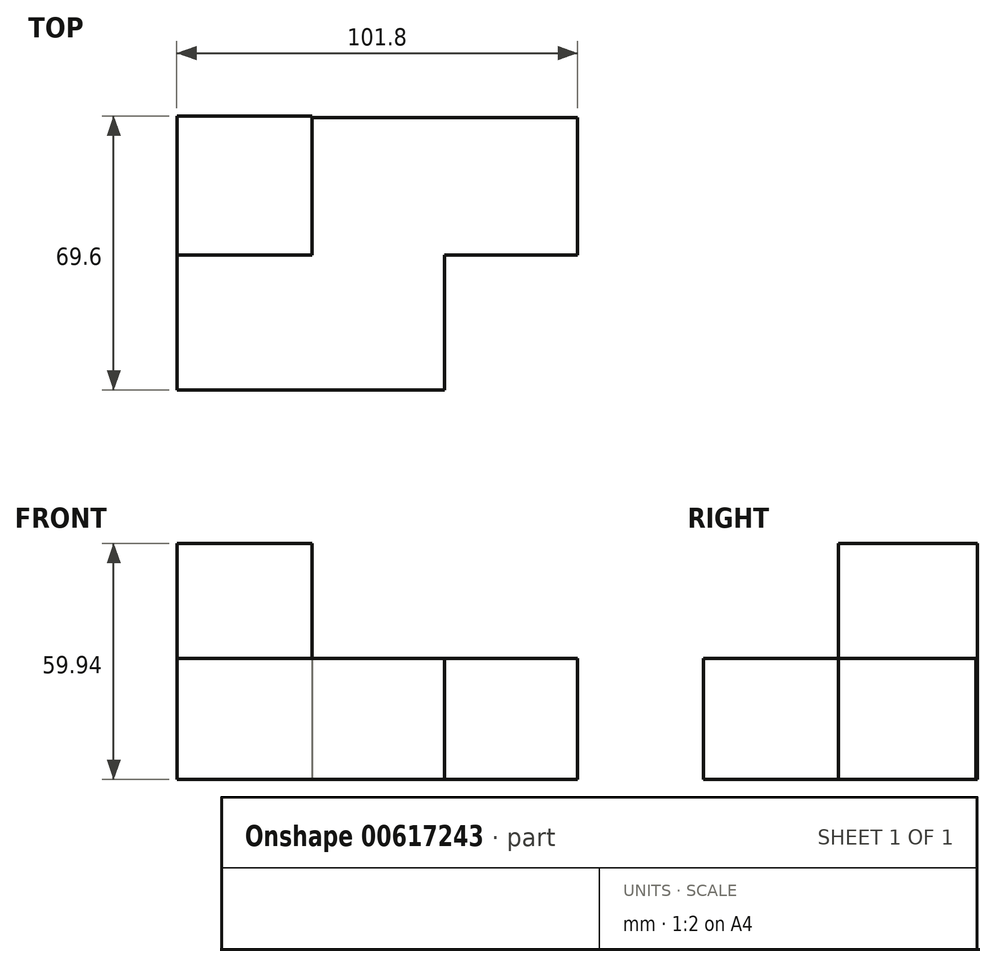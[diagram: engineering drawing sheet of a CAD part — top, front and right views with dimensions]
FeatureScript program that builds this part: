
annotation { "Feature Type Name" : "Feature", "Feature Type Description" : "" }
export const myFeature = defineFeature(function(context is Context, id is Id, definition is map)
    precondition{}
    {
        {
            var Q0;
            Q0=qCreatedBy(makeId("Top.planeOp"),FACE);
            var sketch = newSketch(context, id + "F0", { "sketchPlane" : qUnion([Q0])});
            skLineSegment(sketch, "E0.bottom", {"start": v(-122.91, 56.61) * mm, "end": v(-77.2, 56.61) * mm});
            skLineSegment(sketch, "E0.top", {"start": v(-122.91, -59.5) * mm, "end": v(-77.2, -59.5) * mm});
            skLineSegment(sketch, "E0.left", {"start": v(-122.91, 56.61) * mm, "end": v(-122.91, -59.5) * mm});
            skLineSegment(sketch, "E0.right", {"start": v(-77.2, 56.61) * mm, "end": v(-77.2, -59.5) * mm});
            skLineSegment(sketch, "E1.bottom", {"start": v(-77.2, 56.61) * mm, "end": v(-27.52, 56.61) * mm});
            skLineSegment(sketch, "E1.top", {"start": v(-77.2, -59.5) * mm, "end": v(-27.52, -59.5) * mm});
            skLineSegment(sketch, "E1.right", {"start": v(-27.52, 56.61) * mm, "end": v(-27.52, -59.5) * mm});
            skLineSegment(sketch, "E2.bottom", {"start": v(-27.52, 0) * mm, "end": v(17.94, 0) * mm});
            skLineSegment(sketch, "E2.top", {"start": v(-27.52, -59.5) * mm, "end": v(17.94, -59.5) * mm});
            skLineSegment(sketch, "E2.left", {"start": v(-27.52, 0) * mm, "end": v(-27.52, -59.5) * mm});
            skLineSegment(sketch, "E2.right", {"start": v(17.94, 0) * mm, "end": v(17.94, -59.5) * mm});
            skSolve(sketch);
        }
        {
            var Q0;
            Q0=makeQuery(id+"F0.imprint","IMPRINT",FACE,{"disambiguationData":[TD([[makeQuery(id+"F0.imprint","IMPRINT",EDGE,{"derivedFrom":sQuery(id+"F0.wireOp",EDGE,"E1.bottom")}),-1.0]])]});
            var Q1;
            Q1=makeQuery(id+"F0.imprint","IMPRINT",FACE,{"disambiguationData":[TD([[makeQuery(id+"F0.imprint","IMPRINT",EDGE,{"derivedFrom":sQuery(id+"F0.wireOp",EDGE,"E2.bottom")}),-1.0]])]});
            var Q2;
            Q2=makeQuery(id+"F0.imprint","IMPRINT",FACE,{"disambiguationData":[TD([[makeQuery(id+"F0.imprint","IMPRINT",EDGE,{"derivedFrom":sQuery(id+"F0.wireOp",EDGE,"E0.bottom")}),-1.0]])]});
            extrude(context, id + "F1", {"entities" : qUnion([Q0, Q1, Q2]), "depth" : 38.6 * mm, "offsetDistance" : 25.4 * mm});
        }
        {
            var Q0;
            Q0=makeQuery(id+"F1.opExtrude","CAP_FACE",FACE,{"disambiguationData":[OSD([sQuery(id+"F0.wireOp",EDGE,"E0.bottom"),sQuery(id+"F0.wireOp",EDGE,"E0.top"),sQuery(id+"F0.wireOp",EDGE,"E0.left"),sQuery(id+"F0.wireOp",EDGE,"E1.bottom"),sQuery(id+"F0.wireOp",EDGE,"E1.top"),sQuery(id+"F0.wireOp",EDGE,"E1.right"),sQuery(id+"F0.wireOp",EDGE,"E2.bottom"),sQuery(id+"F0.wireOp",EDGE,"E2.top"),sQuery(id+"F0.wireOp",EDGE,"E2.right")])],"isStart":false});
            var sketch = newSketch(context, id + "F2", { "sketchPlane" : qUnion([Q0])});
            skLineSegment(sketch, "E3.bottom", {"start": v(-122.91, -59.5) * mm, "end": v(-77.24, -59.5) * mm});
            skLineSegment(sketch, "E3.top", {"start": v(-122.91, 0) * mm, "end": v(-77.24, 0) * mm});
            skLineSegment(sketch, "E3.left", {"start": v(-122.91, -59.5) * mm, "end": v(-122.91, 0) * mm});
            skLineSegment(sketch, "E3.right", {"start": v(-77.24, -59.5) * mm, "end": v(-77.24, 0) * mm});
            skSolve(sketch);
        }
        {
            var Q0;
            Q0 = qSketchRegion(id + "F2", true);
            extrude(context, id + "F3", {"entities" : qUnion([Q0]), "operationType" : NewBodyOperationType.ADD, "depth" : 35.3 * mm, "offsetDistance" : 25.4 * mm});
        }
        {
            var Q0;
            Q0=makeQuery(id+"F1.opExtrude","SWEPT_BODY",BODY,{"disambiguationData":[OSD([sQuery(id+"F0.wireOp",EDGE,"E0.bottom"),sQuery(id+"F0.wireOp",EDGE,"E0.top"),sQuery(id+"F0.wireOp",EDGE,"E0.left"),sQuery(id+"F0.wireOp",EDGE,"E1.bottom"),sQuery(id+"F0.wireOp",EDGE,"E1.top"),sQuery(id+"F0.wireOp",EDGE,"E1.right"),sQuery(id+"F0.wireOp",EDGE,"E2.bottom"),sQuery(id+"F0.wireOp",EDGE,"E2.top"),sQuery(id+"F0.wireOp",EDGE,"E2.right")])]});
            deleteBodies(context, id + "F4", {"entities" : qUnion([Q0])});
        }
        {
            var Q0;
            Q0=qCreatedBy(makeId("Top.planeOp"),FACE);
            var sketch = newSketch(context, id + "F5", { "sketchPlane" : qUnion([Q0])});
            skLineSegment(sketch, "E4.bottom", {"start": v(0, 0) * mm, "end": v(-34.22, 0) * mm});
            skLineSegment(sketch, "E4.top", {"start": v(0, 35.28) * mm, "end": v(-34.22, 35.28) * mm});
            skLineSegment(sketch, "E4.left", {"start": v(0, 0) * mm, "end": v(0, 35.28) * mm});
            skLineSegment(sketch, "E4.right", {"start": v(-34.22, 0) * mm, "end": v(-34.22, 35.28) * mm});
            skLineSegment(sketch, "E5.bottom", {"start": v(0, 0) * mm, "end": v(-34.32, 0) * mm});
            skLineSegment(sketch, "E5.top", {"start": v(0, -34.32) * mm, "end": v(-34.32, -34.32) * mm});
            skLineSegment(sketch, "E5.left", {"start": v(0, 0) * mm, "end": v(0, -34.32) * mm});
            skLineSegment(sketch, "E5.right", {"start": v(-34.32, 0) * mm, "end": v(-34.32, -34.32) * mm});
            skLineSegment(sketch, "E6.bottom", {"start": v(0, 0) * mm, "end": v(33.7, 0) * mm});
            skLineSegment(sketch, "E6.top", {"start": v(0, 34.92) * mm, "end": v(33.7, 34.92) * mm});
            skLineSegment(sketch, "E6.left", {"start": v(0, 0) * mm, "end": v(0, 34.92) * mm});
            skLineSegment(sketch, "E6.right", {"start": v(33.7, 0) * mm, "end": v(33.7, 34.92) * mm});
            skLineSegment(sketch, "E7.top", {"start": v(0, -34.32) * mm, "end": v(33.7, -34.32) * mm});
            skLineSegment(sketch, "E7.right", {"start": v(33.7, 0) * mm, "end": v(33.7, -34.32) * mm});
            skPoint(sketch, "E8.oppositeSnap0", {"position": v(16.85, 34.92) * mm});
            skLineSegment(sketch, "E8.bottom", {"start": v(33.7, 0) * mm, "end": v(67.48, 0) * mm});
            skLineSegment(sketch, "E8.top", {"start": v(33.7, 34.92) * mm, "end": v(67.48, 34.92) * mm});
            skLineSegment(sketch, "E8.right", {"start": v(67.48, 0) * mm, "end": v(67.48, 34.92) * mm});
            skSolve(sketch);
        }
        {
            var Q0;
            Q0=makeQuery(id+"F5.imprint","IMPRINT",FACE,{"disambiguationData":[TD([[makeQuery(id+"F5.imprint","IMPRINT",EDGE,{"derivedFrom":sQuery(id+"F5.wireOp",EDGE,"E4.top")}),1.0]])]});
            var Q1;
            Q1=makeQuery(id+"F5.imprint","IMPRINT",FACE,{"disambiguationData":[TD([[makeQuery(id+"F5.imprint","IMPRINT",EDGE,{"derivedFrom":sQuery(id+"F5.wireOp",EDGE,"E5.top")}),-1.0]])]});
            var Q2;
            Q2=makeQuery(id+"F5.imprint","IMPRINT",FACE,{"disambiguationData":[TD([[makeQuery(id+"F5.imprint","IMPRINT",EDGE,{"derivedFrom":sQuery(id+"F5.wireOp",EDGE,"E6.bottom")}),-1.0]])]});
            var Q3;
            Q3=makeQuery(id+"F5.imprint","IMPRINT",FACE,{"disambiguationData":[TD([[makeQuery(id+"F5.imprint","IMPRINT",EDGE,{"derivedFrom":sQuery(id+"F5.wireOp",EDGE,"E6.top")}),-1.0]])]});
            var Q4;
            Q4=makeQuery(id+"F5.imprint","IMPRINT",FACE,{"disambiguationData":[TD([[makeQuery(id+"F5.imprint","IMPRINT",EDGE,{"derivedFrom":sQuery(id+"F5.wireOp",EDGE,"E8.bottom")}),1.0]])]});
            extrude(context, id + "F6", {"entities" : qUnion([Q0, Q1, Q2, Q3, Q4]), "depth" : 30.73 * mm, "offsetDistance" : 25.4 * mm});
        }
        {
            var Q0;
            Q0=makeQuery(id+"F6.opExtrude","CAP_FACE",FACE,{"disambiguationData":[OSD([sQuery(id+"F5.wireOp",EDGE,"E4.top"),sQuery(id+"F5.wireOp",EDGE,"E4.left"),sQuery(id+"F5.wireOp",EDGE,"E4.right"),sQuery(id+"F5.wireOp",EDGE,"E5.bottom"),sQuery(id+"F5.wireOp",EDGE,"E5.top"),sQuery(id+"F5.wireOp",EDGE,"E5.right"),sQuery(id+"F5.wireOp",EDGE,"E6.top"),sQuery(id+"F5.wireOp",EDGE,"E7.top"),sQuery(id+"F5.wireOp",EDGE,"E7.right"),sQuery(id+"F5.wireOp",EDGE,"E8.bottom"),sQuery(id+"F5.wireOp",EDGE,"E8.top"),sQuery(id+"F5.wireOp",EDGE,"E8.right")])],"isStart":false});
            var sketch = newSketch(context, id + "F7", { "sketchPlane" : qUnion([Q0])});
            skLineSegment(sketch, "E9.bottom", {"start": v(-34.22, 35.28) * mm, "end": v(0, 35.28) * mm});
            skLineSegment(sketch, "E9.top", {"start": v(-34.22, 0) * mm, "end": v(0, 0) * mm});
            skLineSegment(sketch, "E9.left", {"start": v(-34.22, 35.28) * mm, "end": v(-34.22, 0) * mm});
            skLineSegment(sketch, "E9.right", {"start": v(0, 35.28) * mm, "end": v(0, 0) * mm});
            skSolve(sketch);
        }
        {
            var Q0;
            {var subQ3=sQuery(id+"F7.wireOp",EDGE,"E9.bottom");Q0=makeQuery(id+"F7.imprint","IMPRINT",FACE,{"disambiguationData":[TD([[makeQuery(id+"F7.imprint","IMPRINT",EDGE,{"derivedFrom":subQ3}),1.0]])]});}
            extrude(context, id + "F8", {"entities" : qUnion([Q0]), "operationType" : NewBodyOperationType.ADD, "depth" : 29.2 * mm, "offsetDistance" : 25.4 * mm});
        }
    });
